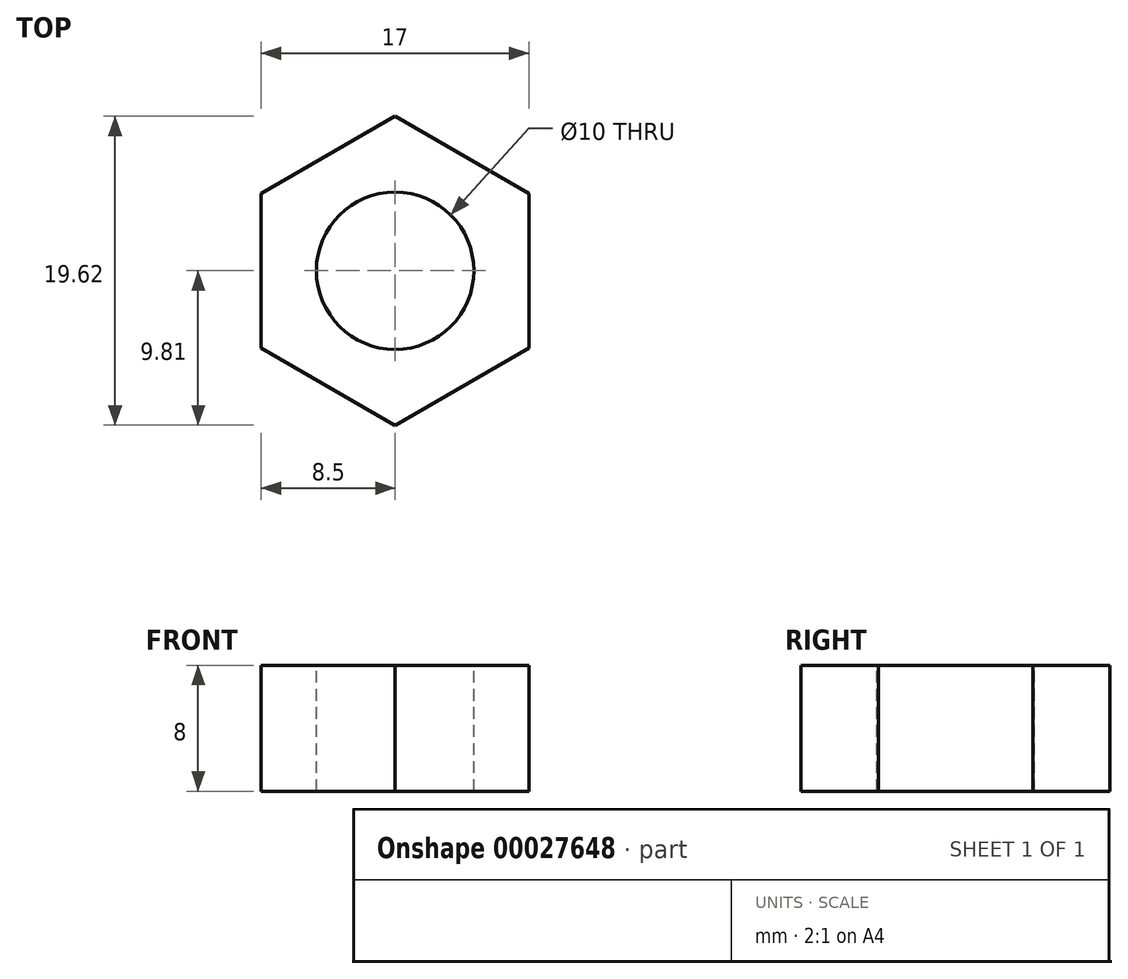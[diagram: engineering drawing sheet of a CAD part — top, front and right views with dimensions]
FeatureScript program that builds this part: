
annotation { "Feature Type Name" : "Feature", "Feature Type Description" : "" }
export const myFeature = defineFeature(function(context is Context, id is Id, definition is map)
    precondition{}
    {
        {
            var Q0;
            Q0=qCreatedBy(makeId("Top.planeOp"),FACE);
            var sketch = newSketch(context, id + "F0", { "sketchPlane" : qUnion([Q0])});
            skCircle(sketch, "E0.cCircle", {"center": v(0, 0) * mm, "radius": 8.5 * mm, "construction": true});
            skLineSegment(sketch, "E0.0", {"start": v(0, -9.81) * mm, "end": v(-8.5, -4.9) * mm});
            skLineSegment(sketch, "E0.1", {"start": v(-8.5, -4.9) * mm, "end": v(-8.5, 4.9) * mm});
            skLineSegment(sketch, "E0.2", {"start": v(-8.5, 4.9) * mm, "end": v(0, 9.81) * mm});
            skLineSegment(sketch, "E0.3", {"start": v(0, 9.81) * mm, "end": v(8.5, 4.9) * mm});
            skLineSegment(sketch, "E0.4", {"start": v(8.5, 4.9) * mm, "end": v(8.5, -4.9) * mm});
            skLineSegment(sketch, "E0.5", {"start": v(8.5, -4.9) * mm, "end": v(0, -9.81) * mm});
            skPoint(sketch, "E0.0.midPoint", {"position": v(-4.25, -7.36) * mm});
            skCircle(sketch, "E1", {"center": v(0, 0) * mm, "radius": 5 * mm});
            skSolve(sketch);
        }
        {
            var Q0;
            Q0=makeQuery(id+"F0.imprint","IMPRINT",FACE,{"disambiguationData":[TD([[makeQuery(id+"F0.imprint","IMPRINT",EDGE,{"derivedFrom":sQuery(id+"F0.wireOp",EDGE,"E0.0")}),-1.0]])]});
            extrude(context, id + "F1", {"entities" : qUnion([Q0]), "oppositeDirection" : true, "depth" : 8 * mm});
        }
    });
